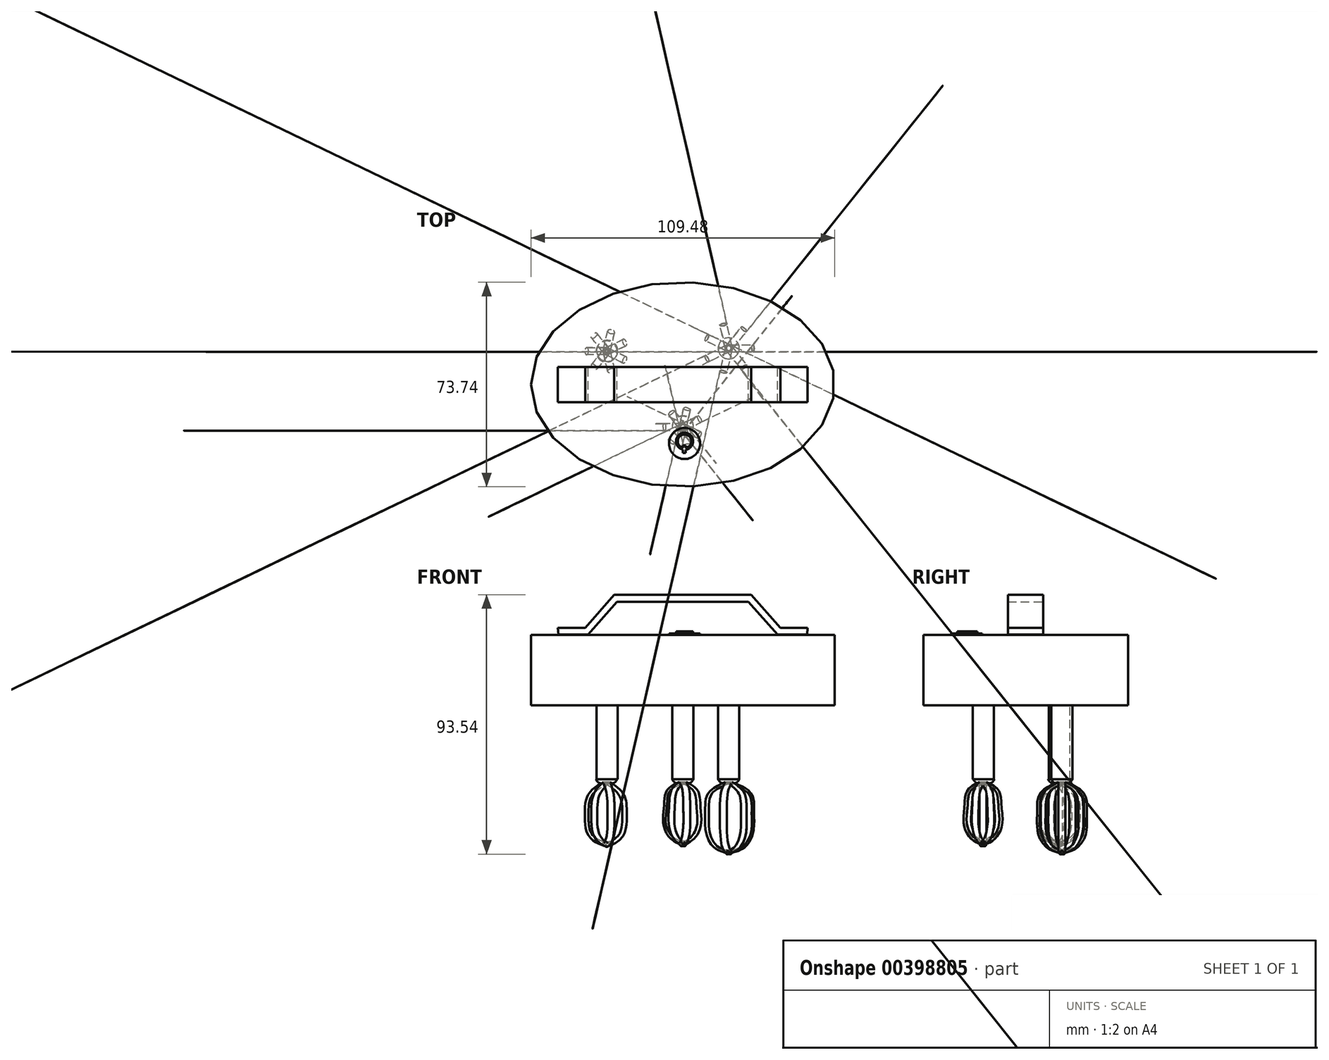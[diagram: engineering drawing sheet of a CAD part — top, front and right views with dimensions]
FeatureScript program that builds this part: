
annotation { "Feature Type Name" : "Feature", "Feature Type Description" : "" }
export const myFeature = defineFeature(function(context is Context, id is Id, definition is map)
    precondition{}
    {
        {
            var Q0;
            Q0=qCreatedBy(makeId("Top.planeOp"),FACE);
            var sketch = newSketch(context, id + "F0", { "sketchPlane" : qUnion([Q0])});
            skEllipse(sketch, "E0", {"center": v(0, 0) * mm, "majorRadius": 54.74 * mm, "minorRadius": 36.87 * mm, "majorAxis": v(-1, 0)});
            skSolve(sketch);
        }
        {
            var Q0;
            Q0=makeQuery(id+"F0.imprint","IMPRINT",FACE,{"disambiguationData":[TD([[makeQuery(id+"F0.imprint","IMPRINT",EDGE,{"derivedFrom":sQuery(id+"F0.wireOp",EDGE,"E0")}),1.0]])]});
            extrude(context, id + "F1", {"entities" : qUnion([Q0]), "depth" : 25.4 * mm});
        }
        {
            var Q0;
            Q0=qCreatedBy(makeId("Front.planeOp"),FACE);
            var sketch = newSketch(context, id + "F2", { "sketchPlane" : qUnion([Q0])});
            skLineSegment(sketch, "E1", {"start": v(-44.85, 25.5) * mm, "end": v(-34.2, 25.5) * mm});
            skLineSegment(sketch, "E2", {"start": v(-34.2, 25.5) * mm, "end": v(-23.7, 37.39) * mm});
            skLineSegment(sketch, "E3", {"start": v(-23.7, 37.39) * mm, "end": v(0, 37.39) * mm});
            skLineSegment(sketch, "E4", {"start": v(0, 37.39) * mm, "end": v(0, 39.85) * mm});
            skLineSegment(sketch, "E5", {"start": v(0, 39.85) * mm, "end": v(-24.7, 39.85) * mm});
            skLineSegment(sketch, "E6", {"start": v(-24.7, 39.85) * mm, "end": v(-35.2, 27.97) * mm});
            skLineSegment(sketch, "E7", {"start": v(-35.2, 27.97) * mm, "end": v(-45.02, 27.97) * mm});
            skLineSegment(sketch, "E8", {"start": v(-45.02, 27.97) * mm, "end": v(-44.85, 25.5) * mm});
            skLineSegment(sketch, "E9", {"start": v(0, 59.42) * mm, "end": v(0, 39.85) * mm, "construction": true});
            skLineSegment(sketch, "E10.trimOffspring", {"start": v(0, 37.39) * mm, "end": v(0, 6.85) * mm, "construction": true});
            skLineSegment(sketch, "E11.MirrorCS", {"start": v(0, 39.85) * mm, "end": v(24.7, 39.85) * mm});
            skLineSegment(sketch, "E12.MirrorCS", {"start": v(23.7, 37.39) * mm, "end": v(0, 37.39) * mm});
            skLineSegment(sketch, "E13.MirrorCS", {"start": v(24.7, 39.85) * mm, "end": v(35.2, 27.97) * mm});
            skLineSegment(sketch, "E14.MirrorCS", {"start": v(34.2, 25.5) * mm, "end": v(23.7, 37.39) * mm});
            skLineSegment(sketch, "E15.MirrorCS", {"start": v(35.2, 27.97) * mm, "end": v(45.02, 27.97) * mm});
            skLineSegment(sketch, "E16.MirrorCS", {"start": v(44.85, 25.5) * mm, "end": v(34.2, 25.5) * mm});
            skLineSegment(sketch, "E17.MirrorCS", {"start": v(45.02, 27.97) * mm, "end": v(44.85, 25.5) * mm});
            skSolve(sketch);
        }
        {
            var Q0;
            Q0=makeQuery(id+"F2.imprint","IMPRINT",FACE,{"disambiguationData":[TD([[makeQuery(id+"F2.imprint","IMPRINT",EDGE,{"derivedFrom":sQuery(id+"F2.wireOp",EDGE,"E1")}),1.0]])]});
            var Q1;
            Q1=makeQuery(id+"F2.imprint","IMPRINT",FACE,{"disambiguationData":[TD([[makeQuery(id+"F2.imprint","IMPRINT",EDGE,{"derivedFrom":sQuery(id+"F2.wireOp",EDGE,"E4")}),-1.0]])]});
            extrude(context, id + "F3", {"entities" : qUnion([Q0, Q1]), "endBound" : BoundingType.SYMMETRIC, "depth" : 12.7 * mm});
        }
        {
            var Q0;
            Q0=makeQuery(id+"F1.opExtrude","CAP_FACE",FACE,{"disambiguationData":[OSD([sQuery(id+"F0.wireOp",EDGE,"E0")])],"isStart":true});
            var sketch = newSketch(context, id + "F4", { "sketchPlane" : qUnion([Q0])});
            skCircle(sketch, "E18", {"center": v(0, 15.27) * mm, "radius": 3.81 * mm});
            skCircle(sketch, "E19", {"center": v(-27.27, -12.16) * mm, "radius": 3.81 * mm});
            skCircle(sketch, "E20", {"center": v(16.54, -13.04) * mm, "radius": 3.81 * mm});
            skSolve(sketch);
        }
        {
            var Q0;
            Q0 = qSketchRegion(id + "F4", true);
            extrude(context, id + "F5", {"entities" : qUnion([Q0]), "operationType" : NewBodyOperationType.ADD, "depth" : 26.67 * mm});
        }
        {
            var Q0;
            Q0=makeQuery(id+"F5.opExtrude","CAP_FACE",FACE,{"disambiguationData":[OSD([sQuery(id+"F4.wireOp",EDGE,"E19")])],"isStart":false});
            cPlane(context, id + "F6", {"entities" : qUnion([Q0]), "cplaneType" : CPlaneType.OFFSET, "offset" : 1.02 * mm, "width" : 152.4 * mm, "height" : 152.4 * mm});
        }
        {
            var Q0;
            Q0=qCreatedBy(id+"F6.planeOp",FACE);
            var sketch = newSketch(context, id + "F7", { "sketchPlane" : qUnion([Q0])});
            skCircle(sketch, "E21", {"center": v(-27.46, -12.02) * mm, "radius": 1.27 * mm});
            skSolve(sketch);
        }
        {
            var Q0;
            Q0=qCreatedBy(makeId("Front.planeOp"),FACE);
            cPlane(context, id + "F8", {"entities" : qUnion([Q0]), "cplaneType" : CPlaneType.OFFSET, "offset" : 11.94 * mm, "oppositeDirection" : true, "width" : 152.4 * mm, "height" : 152.4 * mm});
        }
        {
            var Q0;
            Q0=qCreatedBy(id+"F8.planeOp",FACE);
            var sketch = newSketch(context, id + "F9", { "sketchPlane" : qUnion([Q0])});
            skFitSpline(sketch, "E22", {"points": [v(-27.5, -27.73) * mm, v(-32.27, -31.06) * mm, v(-34.24, -34.45) * mm, v(-34.64, -40.03) * mm, v(-33.63, -46.15) * mm, v(-30.36, -49.14) * mm, v(-27.85, -50.09) * mm], "startDerivative": vector(-28.64, -17.21) * mm, "endDerivative": vector(19.1, -5.74) * mm});
            skSolve(sketch);
        }
        {
            var Q0;
            Q0=makeQuery(id+"F7.imprint","IMPRINT",FACE,{"disambiguationData":[TD([[makeQuery(id+"F7.imprint","IMPRINT",EDGE,{"derivedFrom":sQuery(id+"F7.wireOp",EDGE,"E21")}),1.0]])]});
            var Q1;
            Q1=sQuery(id+"F9.wireOp",EDGE,"E22");
            sweep(context, id + "F10", {"profiles" : qUnion([Q0]), "path" : qUnion([Q1])});
        }
        {
            var Q0;
            Q0=makeQuery(id+"F10.opSweep","SWEPT_BODY",BODY,{"disambiguationData":[OSD([sQuery(id+"F7.wireOp",EDGE,"E21"),sQuery(id+"F9.wireOp",EDGE,"E22")])]});
            var Q1;
            Q1=makeQuery(id+"F10.opSweep","CAP_EDGE",EDGE,{"disambiguationData":[OSD([sQuery(id+"F7.wireOp",EDGE,"E21"),sQuery(id+"F9.wireOp",VERTEX,"E22.start")])],"isStart":true});
            circularPattern(context, id + "F11", {"entities" : qUnion([Q0]), "axis" : qUnion([Q1]), "angle" : 360 * degree, "instanceCount" : 7, "equalSpace" : true});
        }
        {
            var Q0;
            Q0=qCreatedBy(id+"F6.planeOp",FACE);
            var sketch = newSketch(context, id + "F12", { "sketchPlane" : qUnion([Q0])});
            skCircle(sketch, "E23", {"center": v(0, 15.38) * mm, "radius": 1.27 * mm});
            skSolve(sketch);
        }
        {
            var Q0;
            Q0=qCreatedBy(makeId("Front.planeOp"),FACE);
            cPlane(context, id + "F13", {"entities" : qUnion([Q0]), "cplaneType" : CPlaneType.OFFSET, "offset" : 15.5 * mm, "width" : 152.4 * mm, "height" : 152.4 * mm});
        }
        {
            var Q0;
            Q0=qCreatedBy(id+"F13.planeOp",FACE);
            var sketch = newSketch(context, id + "F14", { "sketchPlane" : qUnion([Q0])});
            skFitSpline(sketch, "E24", {"points": [v(0, -27.78) * mm, v(-3.7, -29.67) * mm, v(-5.6, -32.07) * mm, v(-6.22, -36.81) * mm, v(-6.4, -42.87) * mm, v(-3.94, -47.61) * mm, v(0, -49.84) * mm], "startDerivative": vector(-25.41, -10.88) * mm, "endDerivative": vector(25.46, -10.54) * mm});
            skSolve(sketch);
        }
        {
            var Q0;
            Q0=makeQuery(id+"F12.imprint","IMPRINT",FACE,{"disambiguationData":[TD([[makeQuery(id+"F12.imprint","IMPRINT",EDGE,{"derivedFrom":sQuery(id+"F12.wireOp",EDGE,"E23")}),1.0]])]});
            var Q1;
            Q1=sQuery(id+"F14.wireOp",EDGE,"E24");
            sweep(context, id + "F15", {"profiles" : qUnion([Q0]), "path" : qUnion([Q1])});
        }
        {
            var Q0;
            Q0=makeQuery(id+"F15.opSweep","SWEPT_BODY",BODY,{"disambiguationData":[OSD([sQuery(id+"F12.wireOp",EDGE,"E23"),sQuery(id+"F14.wireOp",EDGE,"E24")])]});
            var Q1;
            Q1=makeQuery(id+"F15.opSweep","CAP_EDGE",EDGE,{"disambiguationData":[OSD([sQuery(id+"F12.wireOp",EDGE,"E23"),sQuery(id+"F14.wireOp",VERTEX,"E24.start")])],"isStart":true});
            circularPattern(context, id + "F16", {"entities" : qUnion([Q0]), "axis" : qUnion([Q1]), "angle" : 360 * degree, "instanceCount" : 7, "equalSpace" : true});
        }
        {
            var Q0;
            Q0=qCreatedBy(id+"F6.planeOp",FACE);
            var sketch = newSketch(context, id + "F17", { "sketchPlane" : qUnion([Q0])});
            skCircle(sketch, "E25", {"center": v(16.56, -13.1) * mm, "radius": 1.27 * mm});
            skSolve(sketch);
        }
        {
            var Q0;
            Q0=qCreatedBy(id+"F8.planeOp",FACE);
            var sketch = newSketch(context, id + "F18", { "sketchPlane" : qUnion([Q0])});
            skFitSpline(sketch, "E26", {"points": [v(16.69, -27.77) * mm, v(20.67, -29.46) * mm, v(24.4, -32.47) * mm, v(25.23, -39.16) * mm, v(24.9, -45.9) * mm, v(21.9, -50.87) * mm, v(16.65, -52.98) * mm], "startDerivative": vector(35.73, -12.85) * mm, "endDerivative": vector(-34.17, -8.72) * mm});
            skSolve(sketch);
        }
        {
            var Q0;
            Q0=makeQuery(id+"F17.imprint","IMPRINT",FACE,{"disambiguationData":[TD([[makeQuery(id+"F17.imprint","IMPRINT",EDGE,{"derivedFrom":sQuery(id+"F17.wireOp",EDGE,"E25")}),1.0]])]});
            var Q1;
            Q1=sQuery(id+"F18.wireOp",EDGE,"E26");
            sweep(context, id + "F19", {"profiles" : qUnion([Q0]), "path" : qUnion([Q1])});
        }
        {
            var Q0;
            Q0=makeQuery(id+"F19.opSweep","SWEPT_BODY",BODY,{"disambiguationData":[OSD([sQuery(id+"F17.wireOp",EDGE,"E25"),sQuery(id+"F18.wireOp",EDGE,"E26")])]});
            var Q1;
            Q1=makeQuery(id+"F19.opSweep","CAP_EDGE",EDGE,{"disambiguationData":[OSD([sQuery(id+"F17.wireOp",EDGE,"E25"),sQuery(id+"F18.wireOp",VERTEX,"E26.start")])],"isStart":true});
            circularPattern(context, id + "F20", {"entities" : qUnion([Q0]), "axis" : qUnion([Q1]), "angle" : 360 * degree, "instanceCount" : 7, "equalSpace" : true});
        }
        {
            var Q0;
            Q0=makeQuery(id+"F5.opExtrude","CAP_FACE",FACE,{"disambiguationData":[OSD([sQuery(id+"F4.wireOp",EDGE,"E20")])],"isStart":false});
            var sketch = newSketch(context, id + "F21", { "sketchPlane" : qUnion([Q0])});
            skCircle(sketch, "E27", {"center": v(16.54, -13.04) * mm, "radius": 3.81 * mm});
            skCircle(sketch, "E28", {"center": v(0, 15.07) * mm, "radius": 3.81 * mm});
            skCircle(sketch, "E29", {"center": v(-27.5, -11.9) * mm, "radius": 3.81 * mm});
            skSolve(sketch);
        }
        {
            var Q0;
            Q0 = qSketchRegion(id + "F21", true);
            extrude(context, id + "F22", {"entities" : qUnion([Q0]), "depth" : 1.52 * mm});
        }
        {
            var Q0;
            Q0=makeQuery(id+"F22.opExtrude","CAP_EDGE",EDGE,{"disambiguationData":[OSD([sQuery(id+"F21.wireOp",EDGE,"E27")])],"isStart":false});
            var Q1;
            Q1=makeQuery(id+"F22.opExtrude","CAP_EDGE",EDGE,{"disambiguationData":[OSD([sQuery(id+"F21.wireOp",EDGE,"E29")])],"isStart":false});
            var Q2;
            Q2=makeQuery(id+"F22.opExtrude","CAP_EDGE",EDGE,{"disambiguationData":[OSD([sQuery(id+"F21.wireOp",EDGE,"E28")])],"isStart":false});
            fillet(context, id + "F23", {"entities" : qUnion([Q0, Q1, Q2]), "radius" : 2.27 * mm, "tangentPropagation" : true, "allowEdgeOverflow" : false});
        }
        {
            var Q0;
            Q0=makeQuery(id+"F1.opExtrude","CAP_FACE",FACE,{"disambiguationData":[OSD([sQuery(id+"F0.wireOp",EDGE,"E0")])],"isStart":false});
            var sketch = newSketch(context, id + "F24", { "sketchPlane" : qUnion([Q0])});
            skCircle(sketch, "E30", {"center": v(0.62, -21.29) * mm, "radius": 5.6 * mm});
            skSolve(sketch);
        }
        {
            var Q0;
            Q0 = qSketchRegion(id + "F24", true);
            extrude(context, id + "F25", {"entities" : qUnion([Q0]), "operationType" : NewBodyOperationType.ADD, "depth" : 0.5 * mm});
        }
        {
            var Q0;
            Q0=makeQuery(id+"F25.opExtrude","CAP_FACE",FACE,{"disambiguationData":[OSD([sQuery(id+"F24.wireOp",EDGE,"E30")])],"isStart":false});
            var sketch = newSketch(context, id + "F26", { "sketchPlane" : qUnion([Q0])});
            skCircle(sketch, "E31", {"center": v(0.62, -20.46) * mm, "radius": 3.07 * mm});
            skCircle(sketch, "E32", {"center": v(0.62, -20.46) * mm, "radius": 2.45 * mm});
            skLineSegment(sketch, "E33", {"start": v(0, -22.05) * mm, "end": v(0, -24.62) * mm});
            skLineSegment(sketch, "E34", {"start": v(0, -24.62) * mm, "end": v(1.03, -24.62) * mm});
            skLineSegment(sketch, "E35", {"start": v(1.03, -24.62) * mm, "end": v(1.03, -21.95) * mm});
            skLineSegment(sketch, "E36", {"start": v(1.03, -21.95) * mm, "end": v(0, -22.05) * mm});
            skSolve(sketch);
        }
        {
            var Q0;
            Q0 = qSketchRegion(id + "F26", true);
            var Q1;
            {var subQ5=sQuery(id+"F26.wireOp",EDGE,"E36");Q1=makeQuery(id+"F26.imprint","IMPRINT",FACE,{"disambiguationData":[TD([[makeQuery(id+"F26.imprint","IMPRINT",EDGE,{"derivedFrom":subQ5}),1.0]])]});}
            extrude(context, id + "F27", {"entities" : qUnion([Q0, Q1]), "operationType" : NewBodyOperationType.ADD, "depth" : 0.79 * mm});
        }
    });
